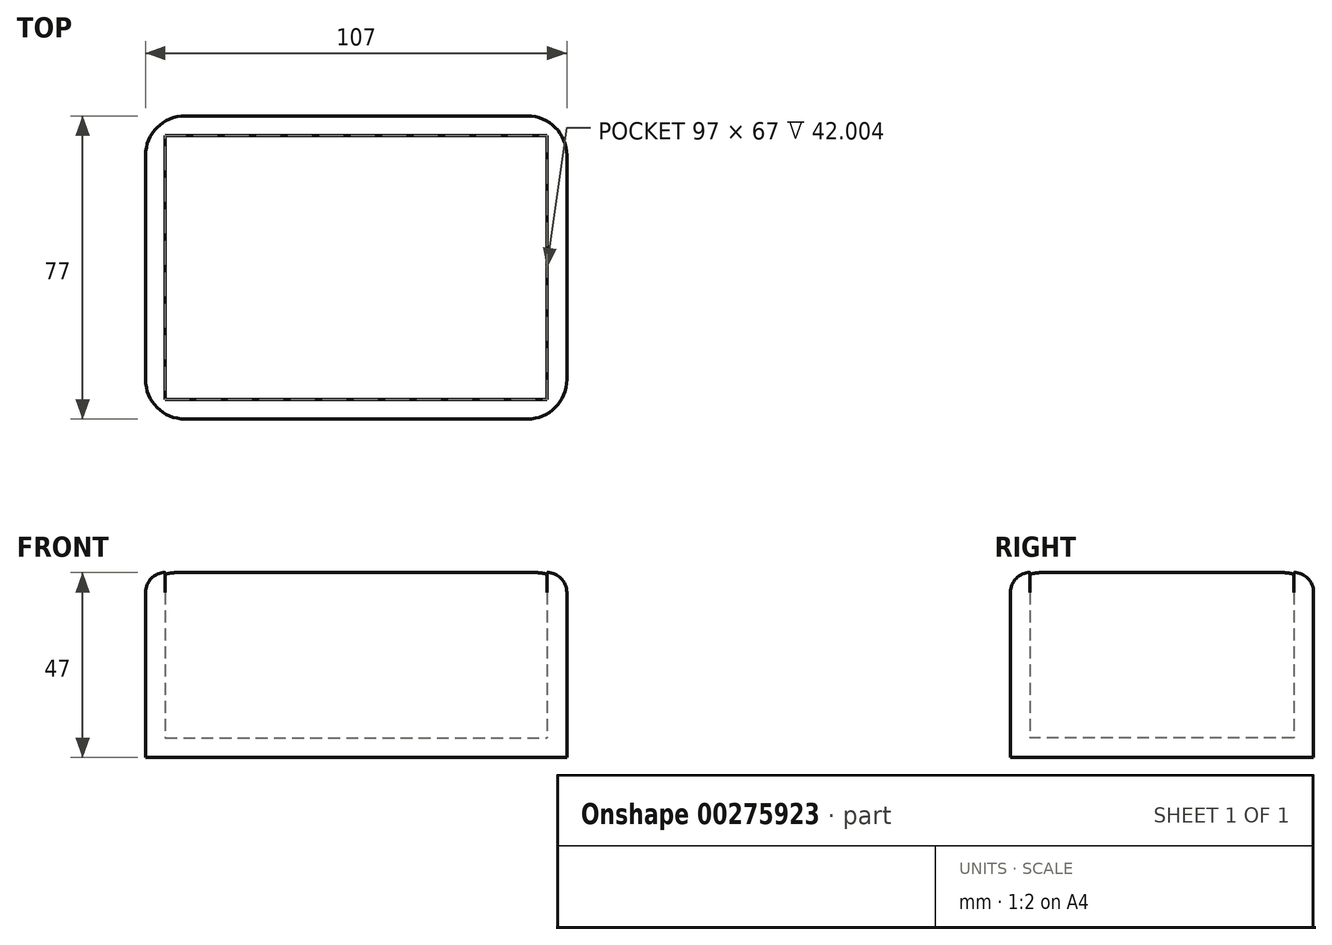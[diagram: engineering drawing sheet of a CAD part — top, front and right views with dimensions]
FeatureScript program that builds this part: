
annotation { "Feature Type Name" : "Feature", "Feature Type Description" : "" }
export const myFeature = defineFeature(function(context is Context, id is Id, definition is map)
    precondition{}
    {
        {
            var Q0;
            Q0=qCreatedBy(makeId("Top.planeOp"),FACE);
            var sketch = newSketch(context, id + "F0", { "sketchPlane" : qUnion([Q0])});
            skLineSegment(sketch, "E0.bottom", {"start": v(-53.5, 38.5) * mm, "end": v(53.5, 38.5) * mm});
            skLineSegment(sketch, "E0.top", {"start": v(-53.5, -38.5) * mm, "end": v(53.5, -38.5) * mm});
            skLineSegment(sketch, "E0.left", {"start": v(-53.5, 38.5) * mm, "end": v(-53.5, -38.5) * mm});
            skLineSegment(sketch, "E0.right", {"start": v(53.5, 38.5) * mm, "end": v(53.5, -38.5) * mm});
            skPoint(sketch, "E0.middle", {"position": v(0, 0) * mm});
            skLineSegment(sketch, "E1.0", {"start": v(-48.5, -33.5) * mm, "end": v(48.5, -33.5) * mm});
            skLineSegment(sketch, "E1.1", {"start": v(-48.5, 33.5) * mm, "end": v(-48.5, -33.5) * mm});
            skLineSegment(sketch, "E1.2", {"start": v(-48.5, 33.5) * mm, "end": v(48.5, 33.5) * mm});
            skLineSegment(sketch, "E1.3", {"start": v(48.5, 33.5) * mm, "end": v(48.5, -33.5) * mm});
            skSolve(sketch);
        }
        {
            var Q0;
            Q0=makeQuery(id+"F0.imprint","IMPRINT",FACE,{"disambiguationData":[TD([[makeQuery(id+"F0.imprint","IMPRINT",EDGE,{"derivedFrom":sQuery(id+"F0.wireOp",EDGE,"E1.0")}),1.0]])]});
            extrude(context, id + "F1", {"entities" : qUnion([Q0]), "depth" : 5 * mm});
        }
        {
            var Q0;
            Q0 = qSketchRegion(id + "F0", true);
            extrude(context, id + "F2", {"entities" : qUnion([Q0]), "operationType" : NewBodyOperationType.ADD, "depth" : 47 * mm});
        }
        {
            var Q0;
            Q0=makeQuery(id+"F2.opExtrude","SWEPT_EDGE",EDGE,{"disambiguationData":[OSD([sQuery(id+"F0.wireOp",EDGE,"E0.bottom"),sQuery(id+"F0.wireOp",EDGE,"E0.left")])]});
            var Q1;
            Q1=makeQuery(id+"F2.opExtrude","SWEPT_EDGE",EDGE,{"disambiguationData":[OSD([sQuery(id+"F0.wireOp",EDGE,"E0.bottom"),sQuery(id+"F0.wireOp",EDGE,"E0.right")])]});
            var Q2;
            Q2=makeQuery(id+"F2.opExtrude","SWEPT_EDGE",EDGE,{"disambiguationData":[OSD([sQuery(id+"F0.wireOp",EDGE,"E0.top"),sQuery(id+"F0.wireOp",EDGE,"E0.right")])]});
            var Q3;
            Q3=makeQuery(id+"F2.opExtrude","SWEPT_EDGE",EDGE,{"disambiguationData":[OSD([sQuery(id+"F0.wireOp",EDGE,"E0.top"),sQuery(id+"F0.wireOp",EDGE,"E0.left")])]});
            fillet(context, id + "F3", {"entities" : qUnion([Q0, Q1, Q2, Q3]), "radius" : 10 * mm, "tangentPropagation" : true, "allowEdgeOverflow" : false});
        }
        {
            var Q0;
            Q0=makeQuery(id+"F2.opExtrude","CAP_EDGE",EDGE,{"disambiguationData":[OSD([sQuery(id+"F0.wireOp",EDGE,"E0.top")])],"isStart":false});
            fillet(context, id + "F4", {"entities" : qUnion([Q0]), "radius" : 5 * mm, "tangentPropagation" : true, "allowEdgeOverflow" : false});
        }
    });
